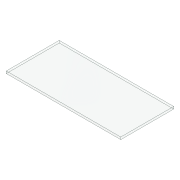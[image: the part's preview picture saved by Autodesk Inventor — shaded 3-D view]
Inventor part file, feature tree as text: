
AUTODESK INVENTOR PART (.ipt)
format: ipt  version: 2020.3 (Build 243373010, 373A)  size: 75,264 bytes
history: native  units: mm
features: extrude x1, sketch x1
ambient origin geometry x8: Origin, YZ Plane, XZ Plane, XY Plane, X Axis, Y Axis, Z Axis, Center Point
bodies: Solid1 (feature_tree)
feature tree (2):
  extrude  "Extrusion1"  Depth=92.5mm
  sketch  "Sketch1"  dims[d0=200.0mm d1=92.5mm d2=4.0mm d3=0.0mm]
